# Revit family: Weitspannkabelleiter WKLG1620 FT,FS FT SO A4.23.08
name_source: partatom
category: Generic Models
revit_build: Autodesk Revit 2017 (Build: 20190508_0315(x64)
units: mm (PartAtom-declared; Revit-internal decimal feet)

## family parameters
Always vertical = Yes
Can host rebar = No
Cut with Voids When Loaded = No
Part Type = Normal
Room Calculation Point = No
Round Connector Dimension = Use Diameter
Shared = No
Work Plane-Based = No

## types (4) — shared parameters
Cut's number = 80
Cut's number 2 = 20
Cut's number 3 = 4
Cut's space = 75 mm
Cut's space 2 = 300 mm
Cut's space 3 = 1500 mm  [stored 4.92126 ft]
Height = 160 mm  [stored 0.524934 ft]
Length = 6000 mm  [stored 19.685 ft]
Manufacturer = OBO Bettermann
URL = http://www.obo-bettermann.com
Width = 200 mm  [stored 0.656168 ft]
Width/2 = 100 mm  [stored 0.328084 ft]

## per-type parameters (varying)
| type | GTIN | Manufacturer Art.No. | Material |
| WKLG 1620 FT | 4012196169399 | 6227120 | Hot-dip galvanised |
| WKLG 1620 FS | 4012196169092 | 6227023 | Strip-galvanised |
| WKLG 1620 FT SO | 4012195888529 | 7189040 | Hot-dip galvanised 85 µm |
| WKLG 1620 A4 | 4012195909965 | 6227170 | Stainless steel, A4 |

note: column(s) folded — value = type name in every type: Article Type

note: [stored X ft] marks values corroborated as IEEE doubles in the binary element streams (Revit-internal decimal feet)

## geometry (parser evidence)
native form markers: Sweep x3
no freeform markers — native parametric forms only
